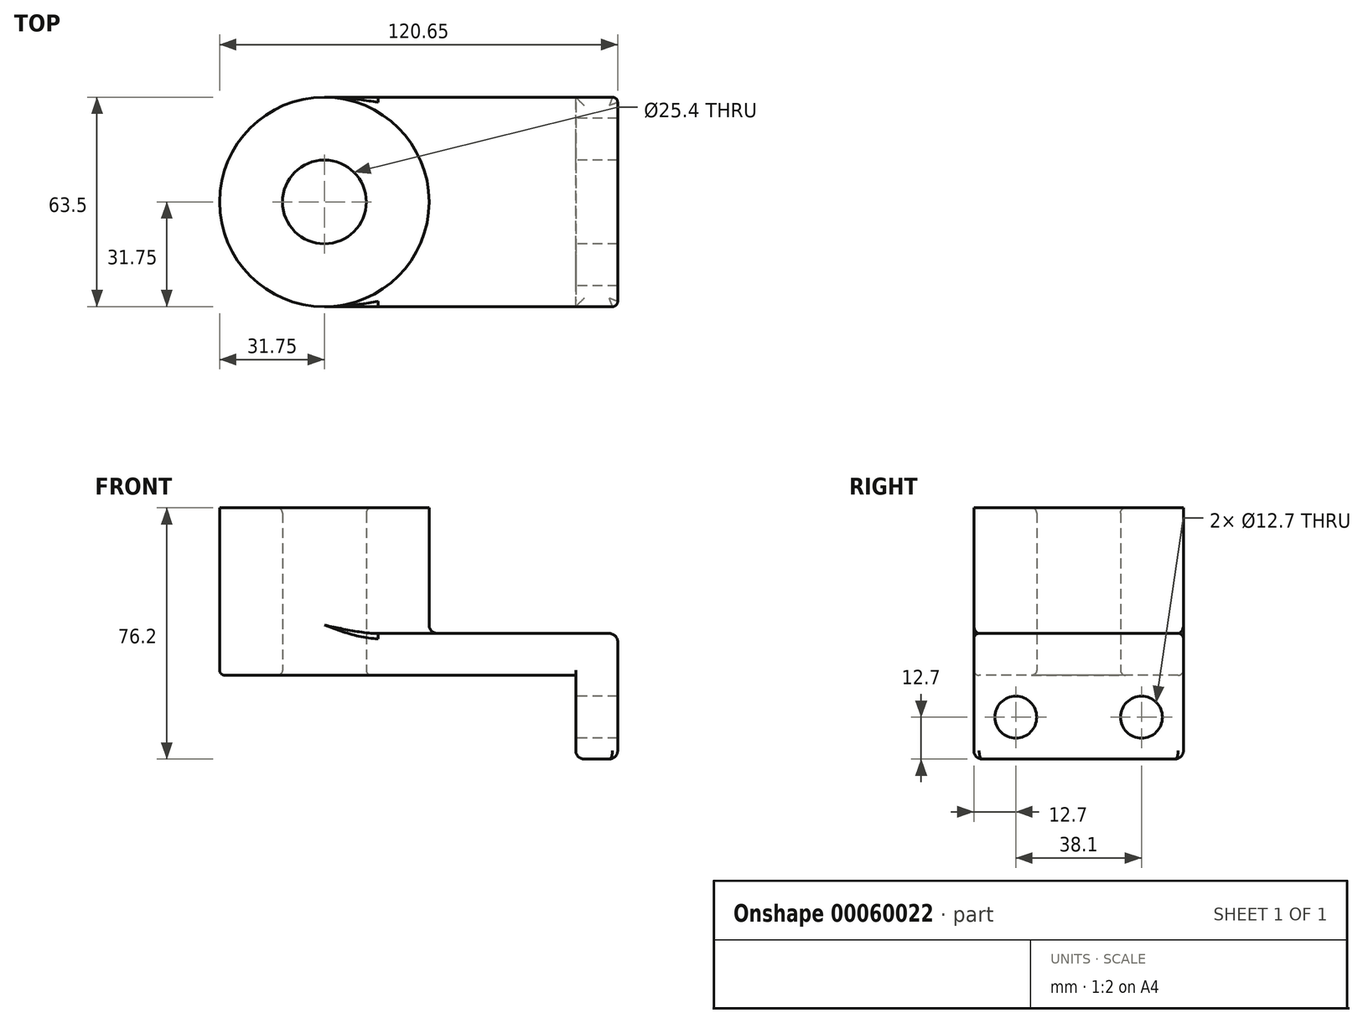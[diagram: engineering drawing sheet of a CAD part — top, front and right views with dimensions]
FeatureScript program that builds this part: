
annotation { "Feature Type Name" : "Feature", "Feature Type Description" : "" }
export const myFeature = defineFeature(function(context is Context, id is Id, definition is map)
    precondition{}
    {
        {
            var Q0;
            Q0=qCreatedBy(makeId("Top.planeOp"),FACE);
            var sketch = newSketch(context, id + "F0", { "sketchPlane" : qUnion([Q0])});
            skLineSegment(sketch, "E0.rect.bottom", {"start": v(-38.1, 31.75) * mm, "end": v(38.1, 31.75) * mm});
            skLineSegment(sketch, "E0.rect.top", {"start": v(-38.1, -31.75) * mm, "end": v(38.1, -31.75) * mm});
            skLineSegment(sketch, "E0.rect.left", {"start": v(-38.1, 31.75) * mm, "end": v(-38.1, -31.75) * mm});
            skLineSegment(sketch, "E0.rect.right", {"start": v(38.1, 31.75) * mm, "end": v(38.1, -31.75) * mm});
            skPoint(sketch, "E0.rect.middle", {"position": v(0, 0) * mm});
            skCircle(sketch, "E1", {"center": v(-38.1, 0) * mm, "radius": 31.75 * mm});
            skCircle(sketch, "E2", {"center": v(-38.1, 0) * mm, "radius": 12.7 * mm});
            skSolve(sketch);
        }
        {
            var Q0;
            {var subQ0=sQuery(id+"F0.wireOp",EDGE,"E0.rect.bottom");Q0=makeQuery(id+"F0.imprint","IMPRINT",FACE,{"disambiguationData":[TD([[makeQuery(id+"F0.imprint","IMPRINT",EDGE,{"derivedFrom":subQ0}),-1.0]])]});}
            var Q1;
            {var subQ1=sQuery(id+"F0.wireOp",EDGE,"E0.rect.left");var subQ3=sQuery(id+"F0.wireOp",EDGE,"E2");var subQ4=makeQuery(id+"F0.imprint","INTERSECT",VERTEX,{"disambiguationData":[OD(0.0)],"derivedFrom":[subQ1,subQ3]});Q1=makeQuery(id+"F0.imprint","IMPRINT",FACE,{"disambiguationData":[TD([[makeQuery(id+"F0.imprint","IMPRINT",EDGE,{"disambiguationData":[TD([[subQ4,1.0]])],"derivedFrom":subQ3}),-1.0]])]});}
            var Q2;
            {var subQ1=sQuery(id+"F0.wireOp",EDGE,"E0.rect.left");var subQ3=sQuery(id+"F0.wireOp",EDGE,"E2");var subQ4=makeQuery(id+"F0.imprint","INTERSECT",VERTEX,{"disambiguationData":[OD(0.0)],"derivedFrom":[subQ1,subQ3]});Q2=makeQuery(id+"F0.imprint","IMPRINT",FACE,{"disambiguationData":[TD([[makeQuery(id+"F0.imprint","IMPRINT",EDGE,{"disambiguationData":[TD([[subQ4,-1.0]])],"derivedFrom":subQ3}),-1.0]])]});}
            extrude(context, id + "F1", {"entities" : qUnion([Q0, Q1, Q2]), "depth" : 12.7 * mm});
        }
        {
            var Q0;
            {var subQ1=sQuery(id+"F0.wireOp",EDGE,"E0.rect.left");var subQ3=sQuery(id+"F0.wireOp",EDGE,"E2");var subQ4=makeQuery(id+"F0.imprint","INTERSECT",VERTEX,{"disambiguationData":[OD(0.0)],"derivedFrom":[subQ1,subQ3]});Q0=makeQuery(id+"F0.imprint","IMPRINT",FACE,{"disambiguationData":[TD([[makeQuery(id+"F0.imprint","IMPRINT",EDGE,{"disambiguationData":[TD([[subQ4,1.0]])],"derivedFrom":subQ3}),-1.0]])]});}
            var Q1;
            {var subQ1=sQuery(id+"F0.wireOp",EDGE,"E0.rect.left");var subQ3=sQuery(id+"F0.wireOp",EDGE,"E2");var subQ4=makeQuery(id+"F0.imprint","INTERSECT",VERTEX,{"disambiguationData":[OD(0.0)],"derivedFrom":[subQ1,subQ3]});Q1=makeQuery(id+"F0.imprint","IMPRINT",FACE,{"disambiguationData":[TD([[makeQuery(id+"F0.imprint","IMPRINT",EDGE,{"disambiguationData":[TD([[subQ4,-1.0]])],"derivedFrom":subQ3}),-1.0]])]});}
            extrude(context, id + "F2", {"entities" : qUnion([Q0, Q1]), "operationType" : NewBodyOperationType.ADD, "depth" : 50.8 * mm});
        }
        {
            var Q0;
            Q0=makeQuery(id+"F1.opExtrude","SWEPT_FACE",FACE,{"disambiguationData":[OSD([sQuery(id+"F0.wireOp",EDGE,"E0.rect.right")])]});
            var sketch = newSketch(context, id + "F3", { "sketchPlane" : qUnion([Q0])});
            skLineSegment(sketch, "E3.bottom", {"start": v(-31.75, 12.7) * mm, "end": v(31.75, 12.7) * mm});
            skLineSegment(sketch, "E3.top", {"start": v(-31.75, -25.4) * mm, "end": v(31.75, -25.4) * mm});
            skLineSegment(sketch, "E3.left", {"start": v(-31.75, 12.7) * mm, "end": v(-31.75, -25.4) * mm});
            skLineSegment(sketch, "E3.right", {"start": v(31.75, 12.7) * mm, "end": v(31.75, -25.4) * mm});
            skCircle(sketch, "E4", {"center": v(-19.05, -12.7) * mm, "radius": 6.35 * mm});
            skLineSegment(sketch, "E5", {"start": v(0, 0) * mm, "end": v(0, -25.4) * mm});
            skCircle(sketch, "E6.MirrorC", {"center": v(19.05, -12.7) * mm, "radius": 6.35 * mm});
            skSolve(sketch);
        }
        {
            var Q0;
            Q0=makeQuery(id+"F3.imprint","IMPRINT",FACE,{"disambiguationData":[TD([[makeQuery(id+"F3.imprint","IMPRINT",EDGE,{"derivedFrom":sQuery(id+"F3.wireOp",EDGE,"E4")}),-1.0]])]});
            var Q1;
            {var subQ5=sQuery(id+"F3.wireOp",EDGE,"E5");Q1=makeQuery(id+"F3.imprint","IMPRINT",FACE,{"disambiguationData":[TD([[makeQuery(id+"F3.imprint","IMPRINT",EDGE,{"derivedFrom":subQ5}),1.0]])]});}
            var Q2;
            {var subQ4=sQuery(id+"F3.wireOp",EDGE,"E3.bottom");Q2=makeQuery(id+"F3.imprint","IMPRINT",FACE,{"disambiguationData":[TD([[makeQuery(id+"F3.imprint","IMPRINT",EDGE,{"derivedFrom":subQ4}),1.0]])]});}
            extrude(context, id + "F4", {"entities" : qUnion([Q0, Q1, Q2]), "operationType" : NewBodyOperationType.ADD, "depth" : 12.7 * mm});
        }
        {
            var Q0;
            {var subQ0=sQuery(id+"F0.wireOp",EDGE,"E1");Q0=makeQuery(id+"F2.boolean.opBoolean","INTERSECT",EDGE,{"derivedFrom":[makeQuery(id+"F1.opExtrude","CAP_FACE",FACE,{"disambiguationData":[OSD([sQuery(id+"F0.wireOp",EDGE,"E0.rect.bottom"),sQuery(id+"F0.wireOp",EDGE,"E0.rect.top"),sQuery(id+"F0.wireOp",EDGE,"E0.rect.right"),subQ0,sQuery(id+"F0.wireOp",EDGE,"E2")])],"isStart":false}),makeQuery(id+"F2.opExtrude","SWEPT_FACE",FACE,{"disambiguationData":[OSD([subQ0])]})]});}
            var Q1;
            Q1=makeQuery(id+"F4.opExtrude","CAP_EDGE",EDGE,{"disambiguationData":[OSD([sQuery(id+"F3.wireOp",EDGE,"E3.bottom")])],"isStart":false});
            var Q2;
            Q2=makeQuery(id+"F4.opExtrude","SWEPT_EDGE",EDGE,{"disambiguationData":[OSD([sQuery(id+"F3.wireOp",EDGE,"E3.top"),sQuery(id+"F3.wireOp",EDGE,"E3.left")])]});
            var Q3;
            Q3=makeQuery(id+"F4.opExtrude","CAP_EDGE",EDGE,{"disambiguationData":[OSD([sQuery(id+"F3.wireOp",EDGE,"E3.top")])],"isStart":false});
            var Q4;
            Q4=makeQuery(id+"F4.opExtrude","SWEPT_EDGE",EDGE,{"disambiguationData":[OSD([sQuery(id+"F3.wireOp",EDGE,"E3.top"),sQuery(id+"F3.wireOp",EDGE,"E3.right")])]});
            var Q5;
            Q5=makeQuery(id+"F4.opExtrude","CAP_EDGE",EDGE,{"disambiguationData":[OSD([sQuery(id+"F3.wireOp",EDGE,"E3.top")])],"isStart":true});
            fillet(context, id + "F5", {"entities" : qUnion([Q0, Q1, Q2, Q3, Q4, Q5]), "radius" : 2.54 * mm, "tangentPropagation" : true, "allowEdgeOverflow" : false});
        }
        {
            var Q0;
            Q0=makeQuery(id+"F4.boolean.opBoolean","MERGE",EDGE,{"derivedFrom":[makeQuery(id+"F1.opExtrude","CAP_EDGE",EDGE,{"disambiguationData":[OSD([sQuery(id+"F0.wireOp",EDGE,"E0.rect.top")])],"isStart":false}),makeQuery(id+"F4.opExtrude","SWEPT_EDGE",EDGE,{"disambiguationData":[OSD([sQuery(id+"F3.wireOp",EDGE,"E3.bottom"),sQuery(id+"F3.wireOp",EDGE,"E3.left")])]})]});
            var Q1;
            Q1=makeQuery(id+"F1.opExtrude","CAP_EDGE",EDGE,{"disambiguationData":[OSD([sQuery(id+"F0.wireOp",EDGE,"E0.rect.top")])],"isStart":true});
            var Q2;
            Q2=makeQuery(id+"F4.boolean.opBoolean","MERGE",EDGE,{"derivedFrom":[makeQuery(id+"F1.opExtrude","CAP_EDGE",EDGE,{"disambiguationData":[OSD([sQuery(id+"F0.wireOp",EDGE,"E0.rect.bottom")])],"isStart":false}),makeQuery(id+"F4.opExtrude","SWEPT_EDGE",EDGE,{"disambiguationData":[OSD([sQuery(id+"F3.wireOp",EDGE,"E3.bottom"),sQuery(id+"F3.wireOp",EDGE,"E3.right")])]})]});
            var Q3;
            Q3=makeQuery(id+"F2.opExtrude","CAP_EDGE",EDGE,{"disambiguationData":[OSD([sQuery(id+"F0.wireOp",EDGE,"E2")])],"isStart":false});
            var Q4;
            Q4=makeQuery(id+"F1.opExtrude","CAP_EDGE",EDGE,{"disambiguationData":[OSD([sQuery(id+"F0.wireOp",EDGE,"E2")])],"isStart":true});
            fillet(context, id + "F6", {"entities" : qUnion([Q0, Q1, Q2, Q3, Q4]), "radius" : 1.59 * mm, "tangentPropagation" : true, "allowEdgeOverflow" : false});
        }
    });
